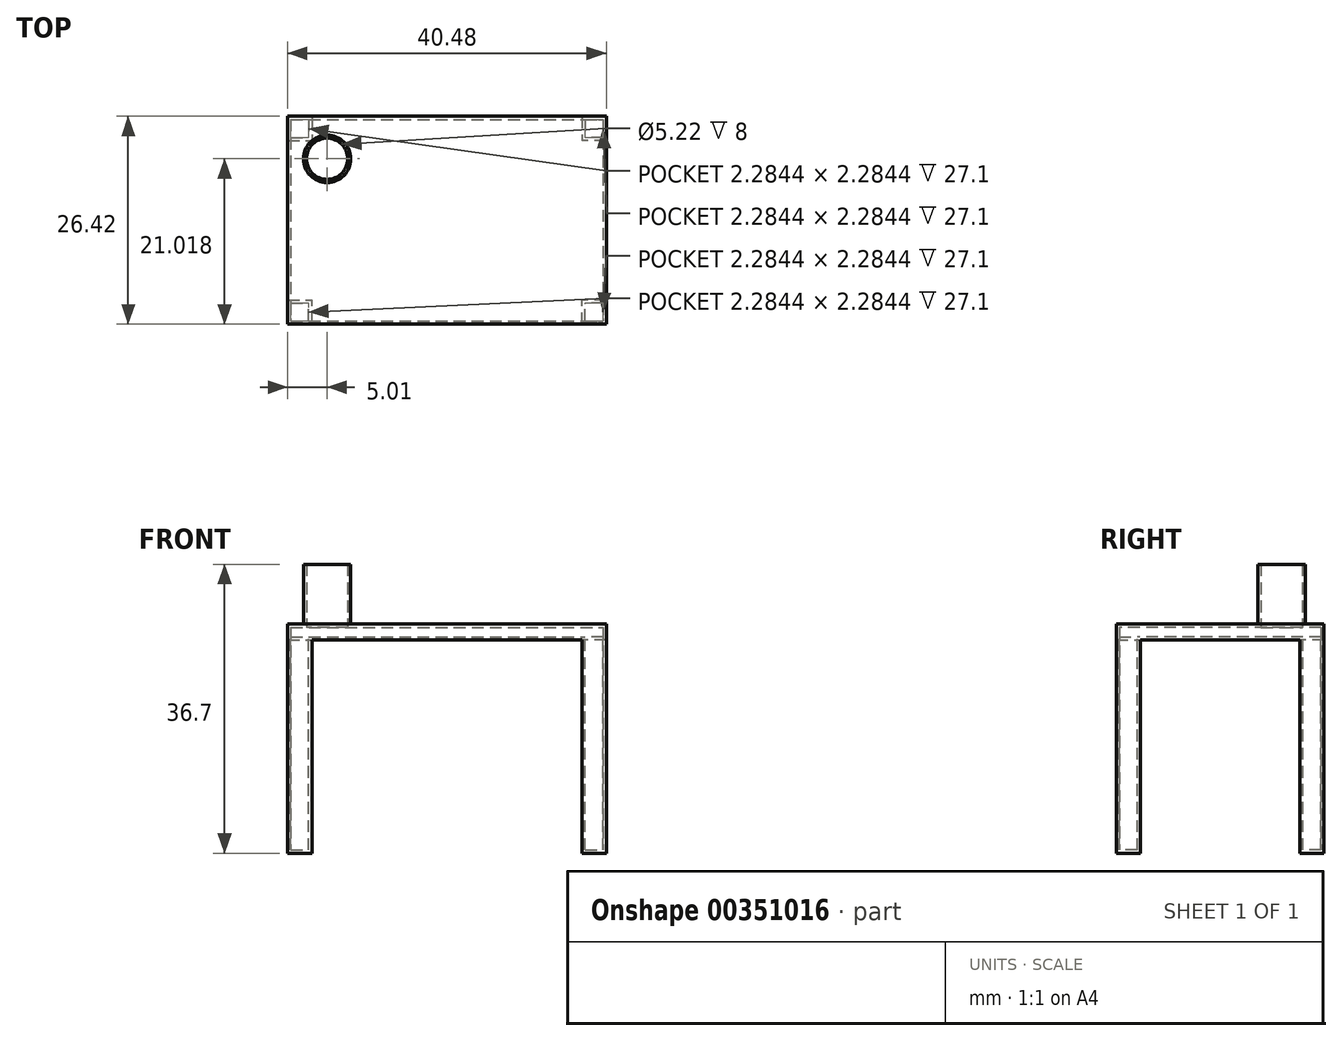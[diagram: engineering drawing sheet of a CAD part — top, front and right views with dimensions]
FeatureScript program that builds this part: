
annotation { "Feature Type Name" : "Feature", "Feature Type Description" : "" }
export const myFeature = defineFeature(function(context is Context, id is Id, definition is map)
    precondition{}
    {
        {
            var Q0;
            Q0=qCreatedBy(makeId("Top.planeOp"),FACE);
            var sketch = newSketch(context, id + "F0", { "sketchPlane" : qUnion([Q0])});
            skLineSegment(sketch, "E0.bottom", {"start": v(-20.24, 13.2) * mm, "end": v(20.24, 13.2) * mm});
            skLineSegment(sketch, "E0.top", {"start": v(-20.24, -13.2) * mm, "end": v(20.24, -13.2) * mm});
            skLineSegment(sketch, "E0.left", {"start": v(-20.24, 13.2) * mm, "end": v(-20.24, -13.2) * mm});
            skLineSegment(sketch, "E0.right", {"start": v(20.24, 13.2) * mm, "end": v(20.24, -13.2) * mm});
            skPoint(sketch, "E0.middle", {"position": v(0, 0) * mm});
            skSolve(sketch);
        }
        {
            var Q0;
            Q0=makeQuery(id+"F0.imprint","IMPRINT",FACE,{"disambiguationData":[TD([[makeQuery(id+"F0.imprint","IMPRINT",EDGE,{"derivedFrom":sQuery(id+"F0.wireOp",EDGE,"E0.bottom")}),-1.0]])]});
            extrude(context, id + "F1", {"entities" : qUnion([Q0]), "depth" : 2 * mm});
        }
        {
            var Q0;
            Q0=makeQuery(id+"F1.opExtrude","CAP_FACE",FACE,{"disambiguationData":[OSD([sQuery(id+"F0.wireOp",EDGE,"E0.bottom"),sQuery(id+"F0.wireOp",EDGE,"E0.top"),sQuery(id+"F0.wireOp",EDGE,"E0.left"),sQuery(id+"F0.wireOp",EDGE,"E0.right")])],"isStart":false});
            var sketch = newSketch(context, id + "F2", { "sketchPlane" : qUnion([Q0])});
            skLineSegment(sketch, "E1.bottom", {"start": v(-20.24, 13.2) * mm, "end": v(-17.16, 13.2) * mm});
            skLineSegment(sketch, "E1.top", {"start": v(-20.24, 10.12) * mm, "end": v(-17.16, 10.12) * mm});
            skLineSegment(sketch, "E1.left", {"start": v(-20.24, 13.2) * mm, "end": v(-20.24, 10.12) * mm});
            skLineSegment(sketch, "E1.right", {"start": v(-17.16, 13.2) * mm, "end": v(-17.16, 10.12) * mm});
            skLineSegment(sketch, "E2.bottom", {"start": v(20.24, 13.2) * mm, "end": v(17.16, 13.2) * mm});
            skLineSegment(sketch, "E2.top", {"start": v(20.24, 10.12) * mm, "end": v(17.16, 10.12) * mm});
            skLineSegment(sketch, "E2.left", {"start": v(20.24, 13.2) * mm, "end": v(20.24, 10.12) * mm});
            skLineSegment(sketch, "E2.right", {"start": v(17.16, 13.2) * mm, "end": v(17.16, 10.12) * mm});
            skLineSegment(sketch, "E3.bottom", {"start": v(20.24, -13.2) * mm, "end": v(17.16, -13.2) * mm});
            skLineSegment(sketch, "E3.top", {"start": v(20.24, -10.12) * mm, "end": v(17.16, -10.12) * mm});
            skLineSegment(sketch, "E3.left", {"start": v(20.24, -13.2) * mm, "end": v(20.24, -10.12) * mm});
            skLineSegment(sketch, "E3.right", {"start": v(17.16, -13.2) * mm, "end": v(17.16, -10.12) * mm});
            skLineSegment(sketch, "E4.bottom", {"start": v(-20.24, -13.2) * mm, "end": v(-17.16, -13.2) * mm});
            skLineSegment(sketch, "E4.top", {"start": v(-20.24, -10.12) * mm, "end": v(-17.16, -10.12) * mm});
            skLineSegment(sketch, "E4.left", {"start": v(-20.24, -13.2) * mm, "end": v(-20.24, -10.12) * mm});
            skLineSegment(sketch, "E4.right", {"start": v(-17.16, -13.2) * mm, "end": v(-17.16, -10.12) * mm});
            skSolve(sketch);
        }
        {
            var Q0;
            Q0 = qSketchRegion(id + "F2", true);
            extrude(context, id + "F3", {"entities" : qUnion([Q0]), "operationType" : NewBodyOperationType.ADD, "oppositeDirection" : true, "depth" : 29.1 * mm});
        }
        {
            var Q0;
            Q0=qCreatedBy(makeId("Top.planeOp"),FACE);
            var sketch = newSketch(context, id + "F4", { "sketchPlane" : qUnion([Q0])});
            skCircle(sketch, "E5", {"center": v(-15.23, 7.8) * mm, "radius": 3.01 * mm});
            skSolve(sketch);
        }
        {
            var Q0;
            Q0 = qSketchRegion(id + "F4", true);
            extrude(context, id + "F5", {"entities" : qUnion([Q0]), "operationType" : NewBodyOperationType.ADD, "depth" : 9.6 * mm});
        }
        {
            var Q0;
            Q0=makeQuery(id+"F5.opExtrude","CAP_FACE",FACE,{"disambiguationData":[OSD([sQuery(id+"F4.wireOp",EDGE,"E5")])],"isStart":false});
            shell(context, id + "F6", {"entities" : qUnion([Q0]), "thickness" : 0.4 * mm});
        }
    });
